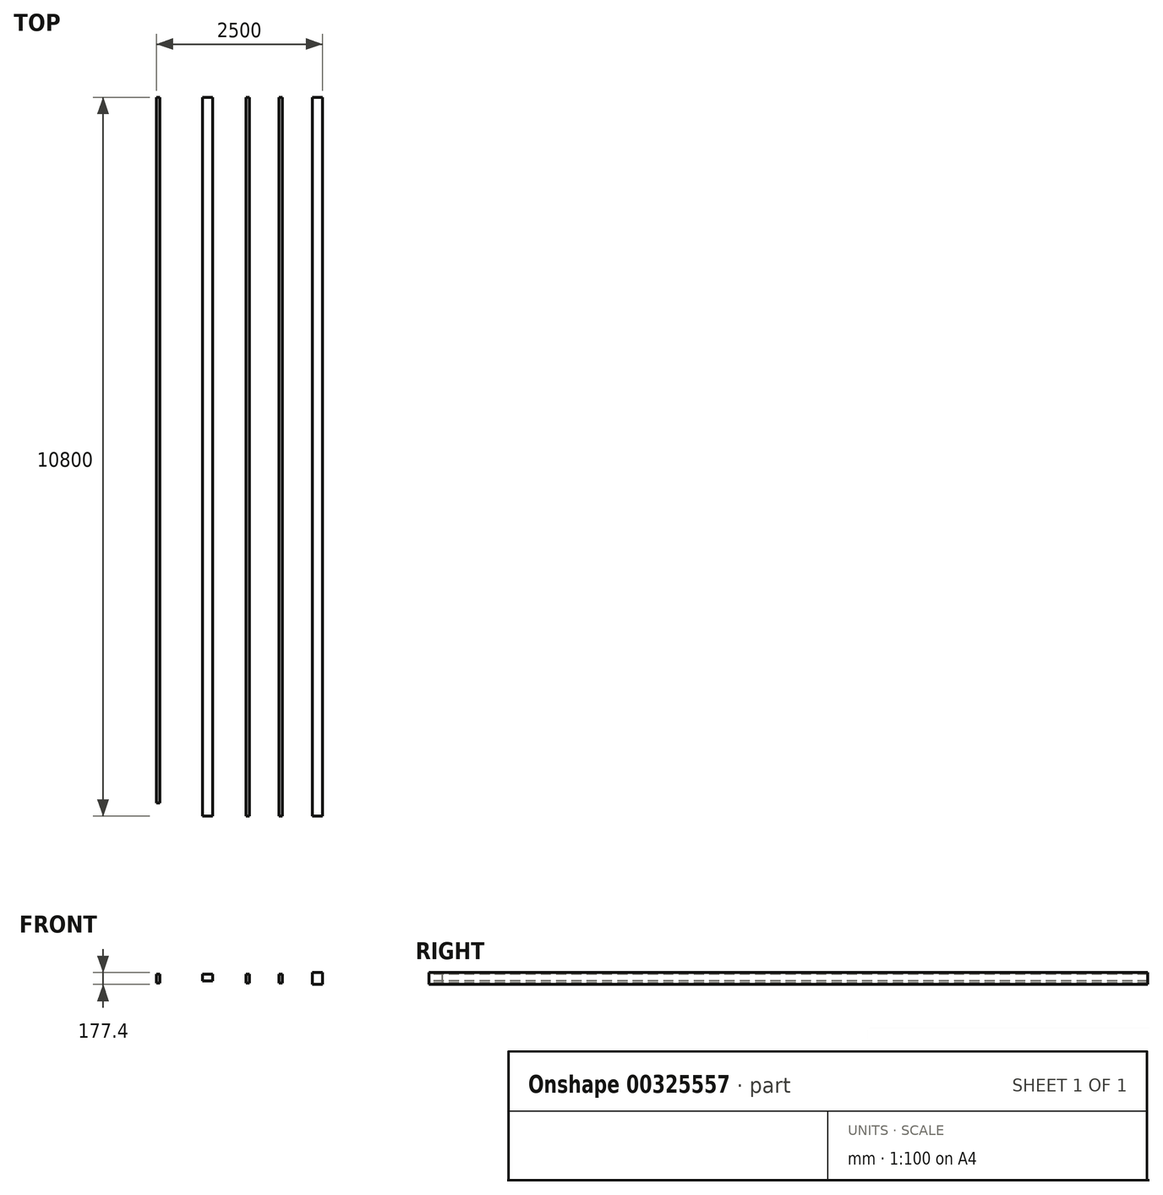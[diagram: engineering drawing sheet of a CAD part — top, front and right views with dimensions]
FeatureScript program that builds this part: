
annotation { "Feature Type Name" : "Feature", "Feature Type Description" : "" }
export const myFeature = defineFeature(function(context is Context, id is Id, definition is map)
    precondition{}
    {
        {
            var Q0;
            Q0=qCreatedBy(makeId("Top.planeOp"),FACE);
            var sketch = newSketch(context, id + "F0", { "sketchPlane" : qUnion([Q0])});
            skLineSegment(sketch, "E0.bottom", {"start": v(-152.4, 10800) * mm, "end": v(0, 10800) * mm});
            skLineSegment(sketch, "E0.top", {"start": v(-152.4, 0) * mm, "end": v(0, 0) * mm});
            skLineSegment(sketch, "E0.left", {"start": v(-152.4, 10800) * mm, "end": v(-152.4, 0) * mm});
            skLineSegment(sketch, "E0.right", {"start": v(0, 10800) * mm, "end": v(0, 0) * mm});
            skSolve(sketch);
        }
        {
            var Q0;
            Q0 = qSketchRegion(id + "F0", true);
            extrude(context, id + "F1", {"entities" : qUnion([Q0]), "depth" : 100 * mm});
        }
        {
            var Q0;
            Q0=makeQuery(id+"F1.opExtrude","CAP_FACE",FACE,{"disambiguationData":[OSD([sQuery(id+"F0.wireOp",EDGE,"E0.bottom"),sQuery(id+"F0.wireOp",EDGE,"E0.top"),sQuery(id+"F0.wireOp",EDGE,"E0.left"),sQuery(id+"F0.wireOp",EDGE,"E0.right")])],"isStart":false});
            var sketch = newSketch(context, id + "F2", { "sketchPlane" : qUnion([Q0])});
            skLineSegment(sketch, "E1.bottom", {"start": v(1500, 10800) * mm, "end": v(1652.4, 10800) * mm});
            skLineSegment(sketch, "E1.top", {"start": v(1500, 0) * mm, "end": v(1652.4, 0) * mm});
            skLineSegment(sketch, "E1.left", {"start": v(1500, 10800) * mm, "end": v(1500, 0) * mm});
            skLineSegment(sketch, "E1.right", {"start": v(1652.4, 10800) * mm, "end": v(1652.4, 0) * mm});
            skSolve(sketch);
        }
        {
            var Q0;
            Q0 = qSketchRegion(id + "F2", true);
            extrude(context, id + "F3", {"entities" : qUnion([Q0]), "oppositeDirection" : true, "depth" : 152.4 * mm});
        }
        {
            var Q0;
            Q0=makeQuery(id+"F1.opExtrude","CAP_FACE",FACE,{"disambiguationData":[OSD([sQuery(id+"F0.wireOp",EDGE,"E0.bottom"),sQuery(id+"F0.wireOp",EDGE,"E0.top"),sQuery(id+"F0.wireOp",EDGE,"E0.left"),sQuery(id+"F0.wireOp",EDGE,"E0.right")])],"isStart":false});
            var sketch = newSketch(context, id + "F4", { "sketchPlane" : qUnion([Q0])});
            skLineSegment(sketch, "E2.bottom", {"start": v(550.8, 10800) * mm, "end": v(500, 10800) * mm});
            skLineSegment(sketch, "E2.top", {"start": v(550.8, 0) * mm, "end": v(500, 0) * mm});
            skLineSegment(sketch, "E2.left", {"start": v(500, 10800) * mm, "end": v(500, 0) * mm});
            skLineSegment(sketch, "E2.right", {"start": v(550.8, 10800) * mm, "end": v(550.8, 0) * mm});
            skLineSegment(sketch, "E3.bottom", {"start": v(1050, 10800) * mm, "end": v(999.2, 10800) * mm});
            skLineSegment(sketch, "E3.top", {"start": v(1050, 0) * mm, "end": v(999.2, 0) * mm});
            skLineSegment(sketch, "E3.left", {"start": v(1050, 10800) * mm, "end": v(1050, 0) * mm});
            skLineSegment(sketch, "E3.right", {"start": v(999.2, 10800) * mm, "end": v(999.2, 0) * mm});
            skLineSegment(sketch, "E4.bottom", {"start": v(-796.8, 10800) * mm, "end": v(-847.6, 10800) * mm});
            skLineSegment(sketch, "E4.top", {"start": v(-796.8, 200.48) * mm, "end": v(-847.6, 200.48) * mm});
            skLineSegment(sketch, "E4.left", {"start": v(-796.8, 10800) * mm, "end": v(-796.8, 200.48) * mm});
            skLineSegment(sketch, "E4.right", {"start": v(-847.6, 10800) * mm, "end": v(-847.6, 200.48) * mm});
            skSolve(sketch);
        }
        {
            var Q0;
            Q0=makeQuery(id+"F4.imprint","IMPRINT",FACE,{"disambiguationData":[TD([[makeQuery(id+"F4.imprint","IMPRINT",EDGE,{"derivedFrom":sQuery(id+"F4.wireOp",EDGE,"E2.bottom")}),1.0]])]});
            extrude(context, id + "F5", {"entities" : qUnion([Q0]), "oppositeDirection" : true, "depth" : 127 * mm});
        }
        {
            var Q0;
            Q0 = qSketchRegion(id + "F4", true);
            extrude(context, id + "F6", {"entities" : qUnion([Q0]), "operationType" : NewBodyOperationType.ADD, "oppositeDirection" : true, "depth" : 130 * mm});
        }
        {
            var Q0;
            Q0 = qSketchRegion(id + "F2", true);
            extrude(context, id + "F7", {"entities" : qUnion([Q0]), "operationType" : NewBodyOperationType.ADD, "depth" : 25 * mm});
        }
    });
